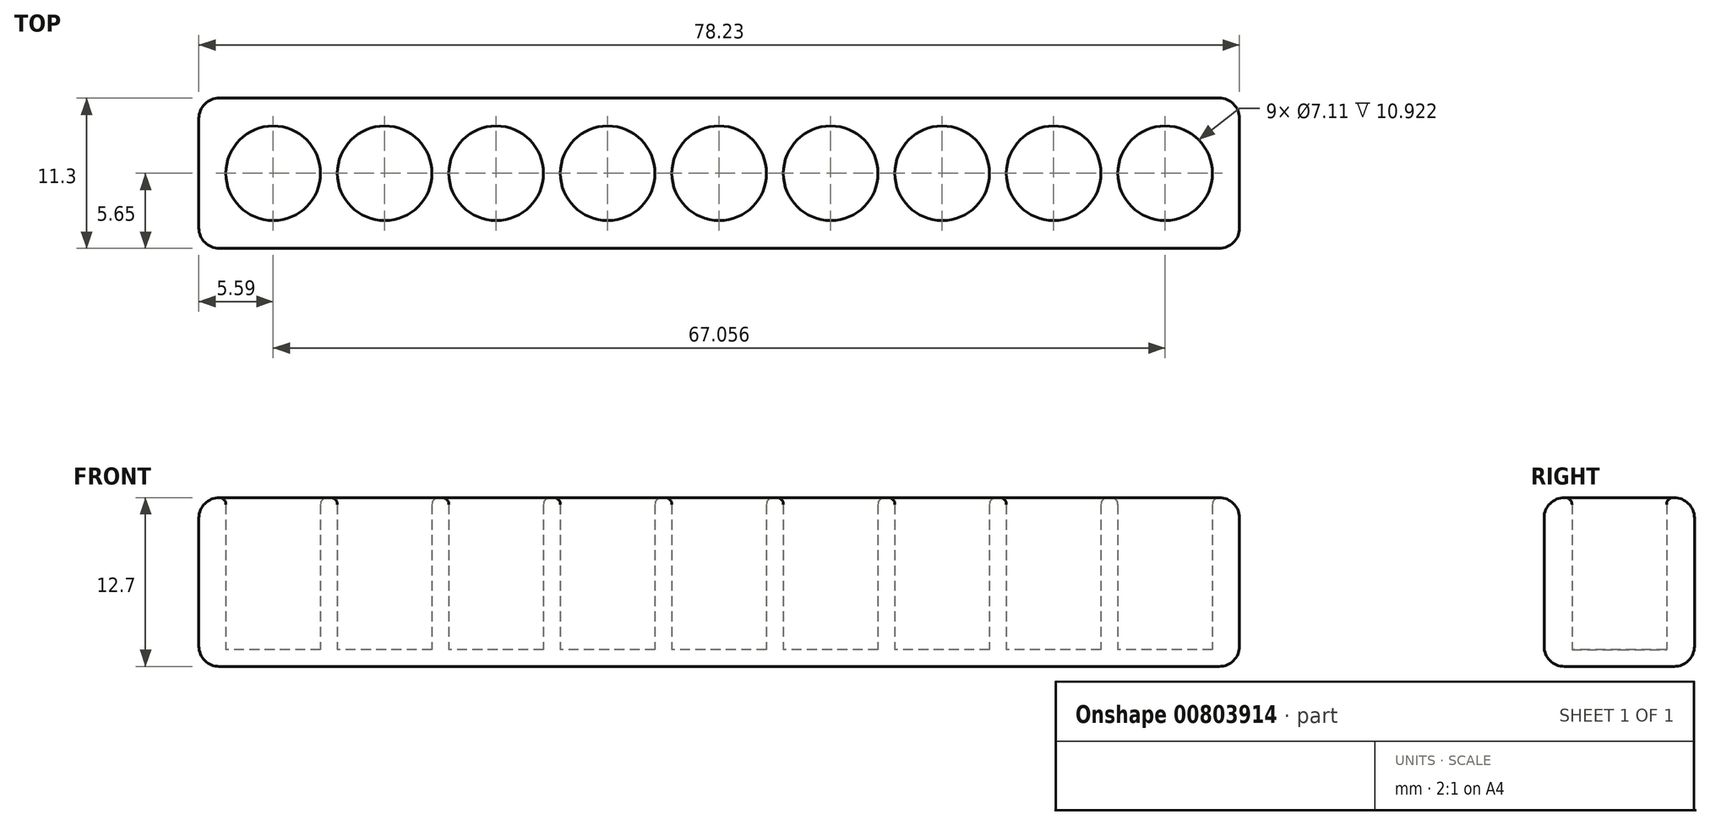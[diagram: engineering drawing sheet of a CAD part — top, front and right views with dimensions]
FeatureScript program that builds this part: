
annotation { "Feature Type Name" : "Feature", "Feature Type Description" : "" }
export const myFeature = defineFeature(function(context is Context, id is Id, definition is map)
    precondition{}
    {
        {
            var Q0;
            Q0=qCreatedBy(makeId("Top.planeOp"),FACE);
            var sketch = newSketch(context, id + "F0", { "sketchPlane" : qUnion([Q0])});
            skLineSegment(sketch, "E0.left", {"start": v(-39.12, 5.6) * mm, "end": v(-39.12, -5.6) * mm});
            skPoint(sketch, "E0.middle", {"position": v(0, 0) * mm});
            skCircle(sketch, "E1", {"center": v(0, 0) * mm, "radius": 3.56 * mm});
            skCircle(sketch, "E2.1.0.0", {"center": v(8.38, 0) * mm, "radius": 3.56 * mm});
            skCircle(sketch, "E2.2.0.0", {"center": v(16.76, 0) * mm, "radius": 3.56 * mm});
            skCircle(sketch, "E2.3.0.0", {"center": v(25.15, 0) * mm, "radius": 3.56 * mm});
            skCircle(sketch, "E2.4.0.0", {"center": v(33.53, 0) * mm, "radius": 3.56 * mm});
            skCircle(sketch, "E2.5.0.0", {"center": v(41.91, 0) * mm, "radius": 3.56 * mm});
            skCircle(sketch, "E2.6.0.0", {"center": v(50.3, 0) * mm, "radius": 3.56 * mm});
            skCircle(sketch, "E2.7.0.0", {"center": v(58.67, 0) * mm, "radius": 3.56 * mm});
            skCircle(sketch, "E2.8.0.0", {"center": v(67.06, 0) * mm, "radius": 3.56 * mm});
            skLineSegment(sketch, "E2.direction1", {"start": v(0, 0) * mm, "end": v(8.38, 0) * mm, "construction": true});
            skLineSegment(sketch, "E3.bottom", {"start": v(-5.59, 5.65) * mm, "end": v(72.64, 5.65) * mm});
            skLineSegment(sketch, "E3.top", {"start": v(-5.59, -5.65) * mm, "end": v(72.64, -5.65) * mm});
            skLineSegment(sketch, "E3.left", {"start": v(-5.59, 5.65) * mm, "end": v(-5.59, -5.65) * mm});
            skLineSegment(sketch, "E3.right", {"start": v(72.64, 5.65) * mm, "end": v(72.64, -5.65) * mm});
            skSolve(sketch);
        }
        {
            var Q0;
            Q0=makeQuery(id+"F0.imprint","IMPRINT",FACE,{"disambiguationData":[TD([[makeQuery(id+"F0.imprint","IMPRINT",EDGE,{"derivedFrom":sQuery(id+"F0.wireOp",EDGE,"E1")}),-1.0]])]});
            extrude(context, id + "F1", {"entities" : qUnion([Q0]), "depth" : 12.7 * mm, "offsetDistance" : 25.4 * mm});
        }
        {
            var Q0;
            Q0=makeQuery(id+"F0.imprint","IMPRINT",FACE,{"disambiguationData":[TD([[makeQuery(id+"F0.imprint","IMPRINT",EDGE,{"derivedFrom":sQuery(id+"F0.wireOp",EDGE,"E1")}),1.0]])]});
            var Q1;
            Q1=makeQuery(id+"F0.imprint","IMPRINT",FACE,{"disambiguationData":[TD([[makeQuery(id+"F0.imprint","IMPRINT",EDGE,{"derivedFrom":sQuery(id+"F0.wireOp",EDGE,"E2.1.0.0")}),1.0]])]});
            var Q2;
            Q2=makeQuery(id+"F0.imprint","IMPRINT",FACE,{"disambiguationData":[TD([[makeQuery(id+"F0.imprint","IMPRINT",EDGE,{"derivedFrom":sQuery(id+"F0.wireOp",EDGE,"E2.2.0.0")}),1.0]])]});
            var Q3;
            Q3=makeQuery(id+"F0.imprint","IMPRINT",FACE,{"disambiguationData":[TD([[makeQuery(id+"F0.imprint","IMPRINT",EDGE,{"derivedFrom":sQuery(id+"F0.wireOp",EDGE,"E2.3.0.0")}),1.0]])]});
            var Q4;
            Q4=makeQuery(id+"F0.imprint","IMPRINT",FACE,{"disambiguationData":[TD([[makeQuery(id+"F0.imprint","IMPRINT",EDGE,{"derivedFrom":sQuery(id+"F0.wireOp",EDGE,"E2.4.0.0")}),1.0]])]});
            var Q5;
            Q5=makeQuery(id+"F0.imprint","IMPRINT",FACE,{"disambiguationData":[TD([[makeQuery(id+"F0.imprint","IMPRINT",EDGE,{"derivedFrom":sQuery(id+"F0.wireOp",EDGE,"E2.5.0.0")}),1.0]])]});
            var Q6;
            Q6=makeQuery(id+"F0.imprint","IMPRINT",FACE,{"disambiguationData":[TD([[makeQuery(id+"F0.imprint","IMPRINT",EDGE,{"derivedFrom":sQuery(id+"F0.wireOp",EDGE,"E2.6.0.0")}),1.0]])]});
            var Q7;
            Q7=makeQuery(id+"F0.imprint","IMPRINT",FACE,{"disambiguationData":[TD([[makeQuery(id+"F0.imprint","IMPRINT",EDGE,{"derivedFrom":sQuery(id+"F0.wireOp",EDGE,"E2.7.0.0")}),1.0]])]});
            var Q8;
            Q8=makeQuery(id+"F0.imprint","IMPRINT",FACE,{"disambiguationData":[TD([[makeQuery(id+"F0.imprint","IMPRINT",EDGE,{"derivedFrom":sQuery(id+"F0.wireOp",EDGE,"E2.8.0.0")}),1.0]])]});
            extrude(context, id + "F2", {"entities" : qUnion([Q0, Q1, Q2, Q3, Q4, Q5, Q6, Q7, Q8]), "operationType" : NewBodyOperationType.ADD, "depth" : 1.27 * mm, "offsetDistance" : 25.4 * mm});
        }
        {
            var Q0;
            Q0=makeQuery(id+"F1.opExtrude","SWEPT_FACE",FACE,{"disambiguationData":[OSD([sQuery(id+"F0.wireOp",EDGE,"E0.top")])]});
            var Q1;
            Q1=makeQuery(id+"F1.opExtrude","SWEPT_FACE",FACE,{"disambiguationData":[OSD([sQuery(id+"F0.wireOp",EDGE,"E0.left")])]});
            var Q2;
            Q2=makeQuery(id+"F1.opExtrude","SWEPT_FACE",FACE,{"disambiguationData":[OSD([sQuery(id+"F0.wireOp",EDGE,"E0.right")])]});
            var Q3;
            Q3=makeQuery(id+"F1.opExtrude","SWEPT_FACE",FACE,{"disambiguationData":[OSD([sQuery(id+"F0.wireOp",EDGE,"E0.bottom")])]});
            var Q4;
            Q4=makeQuery(id+"F1.opExtrude","SWEPT_FACE",FACE,{"disambiguationData":[OSD([sQuery(id+"F0.wireOp",EDGE,"E3.top")])]});
            var Q5;
            Q5=makeQuery(id+"F1.opExtrude","SWEPT_FACE",FACE,{"disambiguationData":[OSD([sQuery(id+"F0.wireOp",EDGE,"E3.left")])]});
            var Q6;
            Q6=makeQuery(id+"F1.opExtrude","SWEPT_FACE",FACE,{"disambiguationData":[OSD([sQuery(id+"F0.wireOp",EDGE,"E3.bottom")])]});
            var Q7;
            Q7=makeQuery(id+"F1.opExtrude","SWEPT_FACE",FACE,{"disambiguationData":[OSD([sQuery(id+"F0.wireOp",EDGE,"E3.right")])]});
            fillet(context, id + "F3", {"entities" : qUnion([Q0, Q1, Q2, Q3, Q4, Q5, Q6, Q7]), "radius" : 1.52 * mm, "tangentPropagation" : true, "allowEdgeOverflow" : false});
        }
        {
            var Q0;
            Q0=makeQuery(id+"F1.opExtrude","CAP_EDGE",EDGE,{"disambiguationData":[OSD([sQuery(id+"F0.wireOp",EDGE,"E1")])],"isStart":false});
            var Q1;
            Q1=makeQuery(id+"F1.opExtrude","CAP_EDGE",EDGE,{"disambiguationData":[OSD([sQuery(id+"F0.wireOp",EDGE,"E2.8.0.0")])],"isStart":false});
            var Q2;
            Q2=makeQuery(id+"F1.opExtrude","CAP_EDGE",EDGE,{"disambiguationData":[OSD([sQuery(id+"F0.wireOp",EDGE,"E2.7.0.0")])],"isStart":false});
            var Q3;
            Q3=makeQuery(id+"F1.opExtrude","CAP_EDGE",EDGE,{"disambiguationData":[OSD([sQuery(id+"F0.wireOp",EDGE,"E2.5.0.0")])],"isStart":false});
            var Q4;
            Q4=makeQuery(id+"F1.opExtrude","CAP_EDGE",EDGE,{"disambiguationData":[OSD([sQuery(id+"F0.wireOp",EDGE,"E2.6.0.0")])],"isStart":false});
            var Q5;
            Q5=makeQuery(id+"F1.opExtrude","CAP_EDGE",EDGE,{"disambiguationData":[OSD([sQuery(id+"F0.wireOp",EDGE,"E2.4.0.0")])],"isStart":false});
            var Q6;
            Q6=makeQuery(id+"F1.opExtrude","CAP_EDGE",EDGE,{"disambiguationData":[OSD([sQuery(id+"F0.wireOp",EDGE,"E2.3.0.0")])],"isStart":false});
            var Q7;
            Q7=makeQuery(id+"F1.opExtrude","CAP_EDGE",EDGE,{"disambiguationData":[OSD([sQuery(id+"F0.wireOp",EDGE,"E2.2.0.0")])],"isStart":false});
            var Q8;
            Q8=makeQuery(id+"F1.opExtrude","CAP_EDGE",EDGE,{"disambiguationData":[OSD([sQuery(id+"F0.wireOp",EDGE,"E2.1.0.0")])],"isStart":false});
            fillet(context, id + "F4", {"entities" : qUnion([Q0, Q1, Q2, Q3, Q4, Q5, Q6, Q7, Q8]), "radius" : 0.5 * mm, "tangentPropagation" : true, "allowEdgeOverflow" : false});
        }
    });
